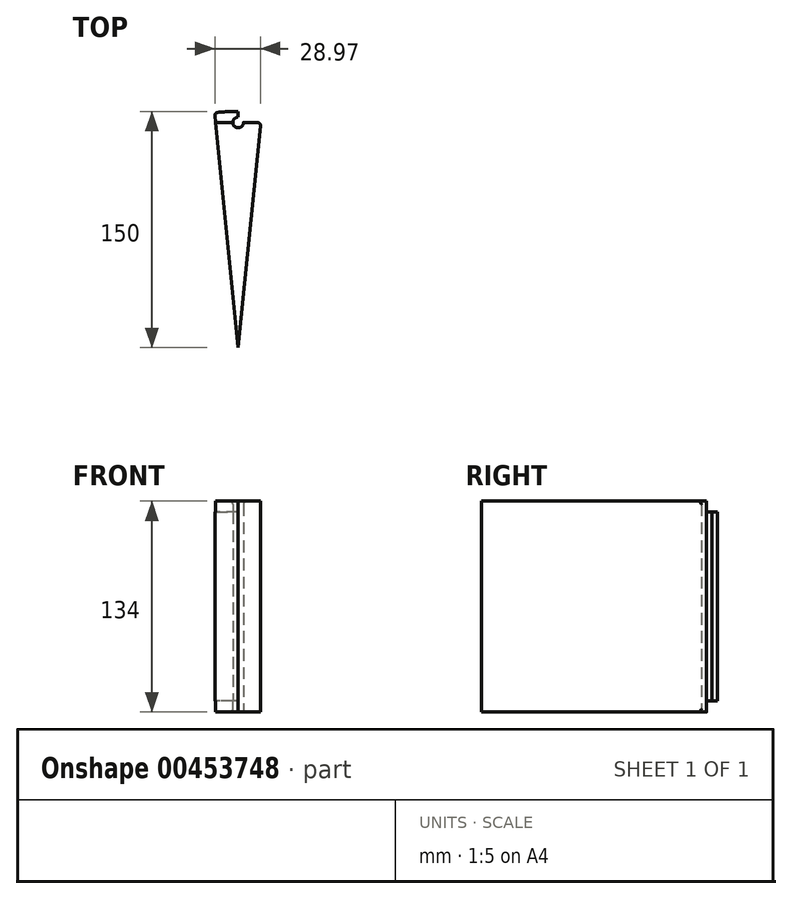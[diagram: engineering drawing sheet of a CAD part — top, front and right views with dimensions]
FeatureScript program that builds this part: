
annotation { "Feature Type Name" : "Feature", "Feature Type Description" : "" }
export const myFeature = defineFeature(function(context is Context, id is Id, definition is map)
    precondition{}
    {
        {
            var Q0;
            Q0=qCreatedBy(makeId("Top.planeOp"),FACE);
            var sketch = newSketch(context, id + "F0", { "sketchPlane" : qUnion([Q0])});
            skArc(sketch, "E0", {"start": v(0, 150) * mm, "mid": v(7.5, 149.81) * mm, "end": v(15, 149.25) * mm});
            skLineSegment(sketch, "E1", {"start": v(15, 149.25) * mm, "end": v(0, 0) * mm});
            skLineSegment(sketch, "E2", {"start": v(0, 150) * mm, "end": v(0, 0) * mm});
            skLineSegment(sketch, "E3", {"start": v(0, 143) * mm, "end": v(15, 143) * mm});
            skLineSegment(sketch, "E4", {"start": v(15, 143) * mm, "end": v(15, 149.25) * mm});
            skCircle(sketch, "E5", {"center": v(0, 143) * mm, "radius": 3.35 * mm});
            skArc(sketch, "E6.MirrorCS", {"start": v(0, 150) * mm, "mid": v(-7.5, 149.81) * mm, "end": v(-15, 149.25) * mm});
            skLineSegment(sketch, "E7.MirrorCS", {"start": v(-15, 149.25) * mm, "end": v(0, 0) * mm});
            skLineSegment(sketch, "E8.MirrorCS", {"start": v(0, 143) * mm, "end": v(-15, 143) * mm});
            skLineSegment(sketch, "E9.MirrorCS", {"start": v(-15, 143) * mm, "end": v(-15, 149.25) * mm});
            skSolve(sketch);
        }
        {
            var Q0;
            {var subQ1=sQuery(id+"F0.wireOp",EDGE,"E6.MirrorCS");Q0=makeQuery(id+"F0.imprint","IMPRINT",FACE,{"disambiguationData":[TD([[makeQuery(id+"F0.imprint","IMPRINT",EDGE,{"derivedFrom":subQ1}),1.0]])]});}
            var Q1;
            {var subQ0=sQuery(id+"F0.wireOp",EDGE,"E5");var subQ1=sQuery(id+"F0.wireOp",EDGE,"E2");var subQ2=makeQuery(id+"F0.imprint","INTERSECT",VERTEX,{"disambiguationData":[OD(0.0)],"derivedFrom":[subQ1,subQ0]});Q1=makeQuery(id+"F0.imprint","IMPRINT",FACE,{"disambiguationData":[TD([[makeQuery(id+"F0.imprint","IMPRINT",EDGE,{"disambiguationData":[TD([[subQ2,-1.0]])],"derivedFrom":subQ1}),1.0]])]});}
            var Q2;
            {var subQ1=sQuery(id+"F0.wireOp",EDGE,"E0");Q2=makeQuery(id+"F0.imprint","IMPRINT",FACE,{"disambiguationData":[TD([[makeQuery(id+"F0.imprint","IMPRINT",EDGE,{"derivedFrom":subQ1}),-1.0]])]});}
            var Q3;
            {var subQ0=sQuery(id+"F0.wireOp",EDGE,"E5");var subQ1=sQuery(id+"F0.wireOp",EDGE,"E2");var subQ2=makeQuery(id+"F0.imprint","INTERSECT",VERTEX,{"disambiguationData":[OD(0.0)],"derivedFrom":[subQ1,subQ0]});Q3=makeQuery(id+"F0.imprint","IMPRINT",FACE,{"disambiguationData":[TD([[makeQuery(id+"F0.imprint","IMPRINT",EDGE,{"disambiguationData":[TD([[subQ2,-1.0]])],"derivedFrom":subQ1}),-1.0]])]});}
            extrude(context, id + "F1", {"entities" : qUnion([Q0, Q1, Q2, Q3]), "depth" : 120 * mm});
        }
        {
            var Q0;
            {var subQ0=sQuery(id+"F0.wireOp",EDGE,"E5");var subQ1=sQuery(id+"F0.wireOp",EDGE,"E2");var subQ2=makeQuery(id+"F0.imprint","INTERSECT",VERTEX,{"disambiguationData":[OD(0.0)],"derivedFrom":[subQ1,subQ0]});Q0=makeQuery(id+"F0.imprint","IMPRINT",FACE,{"disambiguationData":[TD([[makeQuery(id+"F0.imprint","IMPRINT",EDGE,{"disambiguationData":[TD([[subQ2,-1.0]])],"derivedFrom":subQ1}),1.0]])]});}
            var Q1;
            {var subQ0=sQuery(id+"F0.wireOp",EDGE,"E5");var subQ1=sQuery(id+"F0.wireOp",EDGE,"E2");var subQ2=makeQuery(id+"F0.imprint","INTERSECT",VERTEX,{"disambiguationData":[OD(0.0)],"derivedFrom":[subQ1,subQ0]});Q1=makeQuery(id+"F0.imprint","IMPRINT",FACE,{"disambiguationData":[TD([[makeQuery(id+"F0.imprint","IMPRINT",EDGE,{"disambiguationData":[TD([[subQ2,-1.0]])],"derivedFrom":subQ1}),-1.0]])]});}
            extrude(context, id + "F2", {"entities" : qUnion([Q0, Q1]), "operationType" : NewBodyOperationType.ADD, "oppositeDirection" : true, "depth" : 7 * mm});
        }
        {
            var Q0;
            Q0=makeQuery(id+"F2.opExtrude","CAP_FACE",FACE,{"disambiguationData":[OSD([sQuery(id+"F0.wireOp",EDGE,"E5")])],"isStart":false});
            extrude(context, id + "F3", {"entities" : qUnion([Q0]), "operationType" : NewBodyOperationType.ADD, "oppositeDirection" : true, "depth" : 134 * mm});
        }
        {
            var Q0;
            Q0=makeQuery(id+"F2.opExtrude","CAP_EDGE",EDGE,{"disambiguationData":[OSD([sQuery(id+"F0.wireOp",EDGE,"E5")])],"isStart":false});
            var Q1;
            Q1=makeQuery(id+"F3.opExtrude","CAP_EDGE",EDGE,{"disambiguationData":[OSD([sQuery(id+"F0.wireOp",EDGE,"E5")])],"isStart":false});
            var Q2;
            Q2=makeQuery(id+"F1.opExtrude","SWEPT_EDGE",EDGE,{"disambiguationData":[OSD([sQuery(id+"F0.wireOp",EDGE,"E6.MirrorCS"),sQuery(id+"F0.wireOp",EDGE,"E7.MirrorCS"),sQuery(id+"F0.wireOp",EDGE,"E9.MirrorCS")])]});
            var Q3;
            Q3=makeQuery(id+"F1.opExtrude","SWEPT_EDGE",EDGE,{"disambiguationData":[OSD([sQuery(id+"F0.wireOp",EDGE,"E0"),sQuery(id+"F0.wireOp",EDGE,"E1"),sQuery(id+"F0.wireOp",EDGE,"E4")])]});
            fillet(context, id + "F4", {"entities" : qUnion([Q0, Q1, Q2, Q3]), "radius" : 2 * mm, "tangentPropagation" : true, "allowEdgeOverflow" : false});
        }
    });
